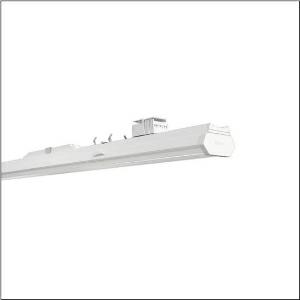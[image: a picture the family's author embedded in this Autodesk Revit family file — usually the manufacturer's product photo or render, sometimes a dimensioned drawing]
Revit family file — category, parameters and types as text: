
# Revit family: licross_r__21_performance_mo_52td16mn4a5g_2767
name_source: partatom
category: Lighting Fixtures
units: mm (PartAtom-declared; Revit-internal decimal feet)

## family parameters
Cut with Voids When Loaded = No
Host = Face
Light Source = No
Part Type = Normal
Room Calculation Point = No
Round Connector Dimension = Use Diameter
Shared = No

## types (1)
- --- (1 x LED, 10890 lm, 60.5 W, 4000K)
    Apparent Load = 61 VA
    CIE Flux Codes = 66 88 96 79 100
    Color Rendering = 80
    Color Temperature = 4000K
    Default Elevation = 1800 mm
    Description = Licross® 21 Performance MO, luminaire insert, of sheet steel, galvanised, coil coated, white, length: 1.500mm, width: 120mm, height: 123mm, LED rated luminous flux: 10.890lm, light colour: 840, control gear: ON/OFF Multilumen, control gear: ECG Multilumen, with plug, 3-pole, with phase selection, mains connection: 220..240V, AC, 50/60Hz, halogen-free wiring, primary light control with lens, of plastic, primary optical cover: cover, of PMMA, light emission: direct/indirect distribution, primary light characteristic: symmetric, protection rating (complete): IP54, insulation class (complete): insulation class I (protective earthing), certification: CE, ENEC, UKCA, protection symbol: D if used in an environment with non-conductive dust loads with corresponding accessories, impact resistance: IK06, permissible ambient temperature for indoor applications: -35..+45°C, corresponds to IFS (International Featured Standards) requirements for safety and quality in the food industry, reducing of maximum allowable ambient temperature of 5°C with ceiling mounting, LABS conformity tested according to VDMA 24364:2018-05, packaging unit: 1 piece
    Height = 114 mm
    Lamp = 1 x LED
    Lamp Light Flux = 10890 lm
    Lamp Power = 60.5 W
    Lamp count = 1
    Length = 1500 mm
    Luminous efficacy = 180 lm/W
    Manufacturer = Siteco
    ModVariant = No
    Model = 52TD16MN4A5G
    Mounting Place = Ceiling
    Mounting Type = Pendant
    Number of Poles = 1
    OnlyDefault = Yes
    Power Factor = 1
    Product Name = Licross® 21 Performance MO
    Product group = luminaire insert
    ProductGroupID = 902
    Protection Class = Protection class I
    Protection Degree = IP 54
    RLX_Detail_Level = 1
    RlxData = <blob elided: 29689 chars, md5=0a8fae5b>
    Socket = socket
    Standby Power = 0 W
    System Light Flux = 10890 lm
    System Power = 61 W
    Type Comments = factory setting: luminous flux: 100 % | (A | C | E) | 140 mA
    Type Image = l_1256148.jpg
    URL = http://relux.com
    VarID = @adj_017687
    Voltage = 0 V
    Weight = 0.00 kg
    Width = 120 mm

## geometry (parser evidence)
native form markers: Blend x4, Sweep x12
no freeform markers — native parametric forms only
